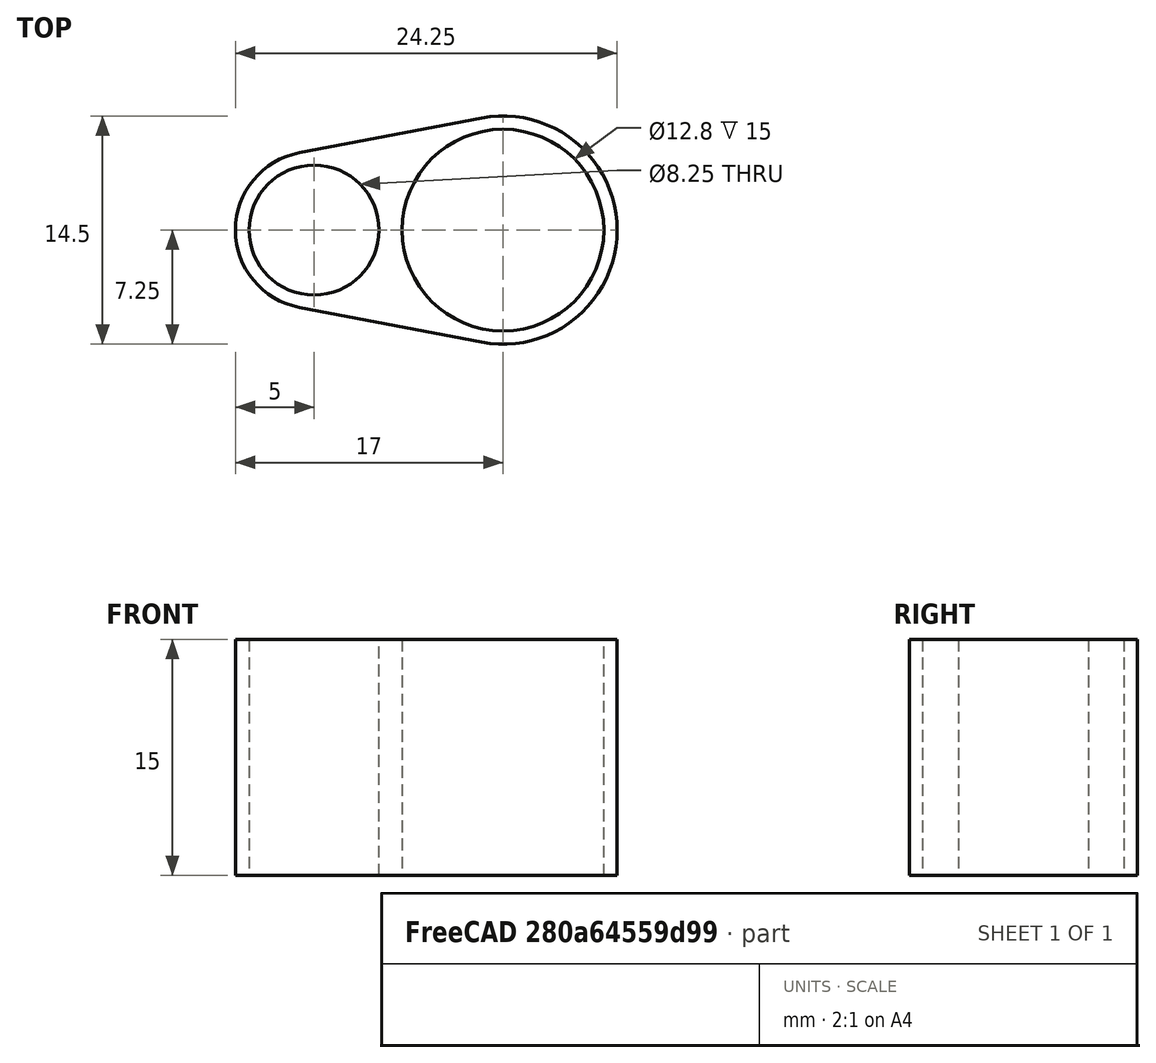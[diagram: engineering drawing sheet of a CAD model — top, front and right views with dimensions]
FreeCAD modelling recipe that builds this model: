
FCSTD DOCUMENT  (FreeCAD 0.18R16110 (Git))
Label: Plug_mount
License: All rights reserved
LicenseURL: http://en.wikipedia.org/wiki/All_rights_reserved
objects: Sketcher::SketchObject×1, PartDesign::Pad×1, PartDesign::Body×1
note: 4 computed .brp shape members not serialized (recipe doc carries the construction recipe); baked Part::Feature solids carry a one-line shape summary decoded from their .brp

FEATURE [Sketcher::SketchObject] Sketch
  MapMode = 5
  Support = -> [XY_Plane]
  sketch-geometry (6):
    g0: ArcOfCircle CenterX=0 CenterY=0 CenterZ=0 NormalX=0 NormalY=0 NormalZ=1 AngleXU=0 Radius=5 StartAngle=1.75941 EndAngle=4.52377
    g1: ArcOfCircle CenterX=12 CenterY=0 CenterZ=0 NormalX=0 NormalY=0 NormalZ=1 AngleXU=0 Radius=7.25 StartAngle=4.52377 EndAngle=8.0426
    g2: LineSegment StartX=-0.9375 StartY=-4.91132 StartZ=0 EndX=10.6406 EndY=-7.12142 EndZ=0
    g3: LineSegment StartX=-0.9375 StartY=4.91132 StartZ=0 EndX=10.6406 EndY=7.12142 EndZ=0
    g4: Circle CenterX=0 CenterY=0 CenterZ=0 NormalX=0 NormalY=0 NormalZ=1 AngleXU=0 Radius=4.125
    g5: Circle CenterX=12 CenterY=0 CenterZ=0 NormalX=0 NormalY=0 NormalZ=1 AngleXU=0 Radius=6.4
  constraints (13):
    c: Tangent(g0,g3) = 1.5708
    c: Tangent(g0,g2) = -1.5708
    c: Tangent(g2,g1) = -1.5708
    c: Tangent(g3,g1) = 1.5708
    c: Coincident(g0,g4)
    c: Coincident(g0,g-1)
    c: Diameter(g4) = 8.25
    c: Diameter(g5) = 12.8
    c: DistanceX(g0,g1) = 12
    c: Coincident(g5,g1)
    c: PointOnObject(g1,g-1)
    c: Diameter(g1) = 14.5
    c: Diameter(g0) = 10
FEATURE [PartDesign::Pad] Pad
  Length = 15
  Length2 = 100
  Profile = -> Sketch
  Type = 0
FEATURE [PartDesign::Body] Body
  Group = -> [Sketch,Pad]
  Origin = -> Origin
  Tip = -> Pad
